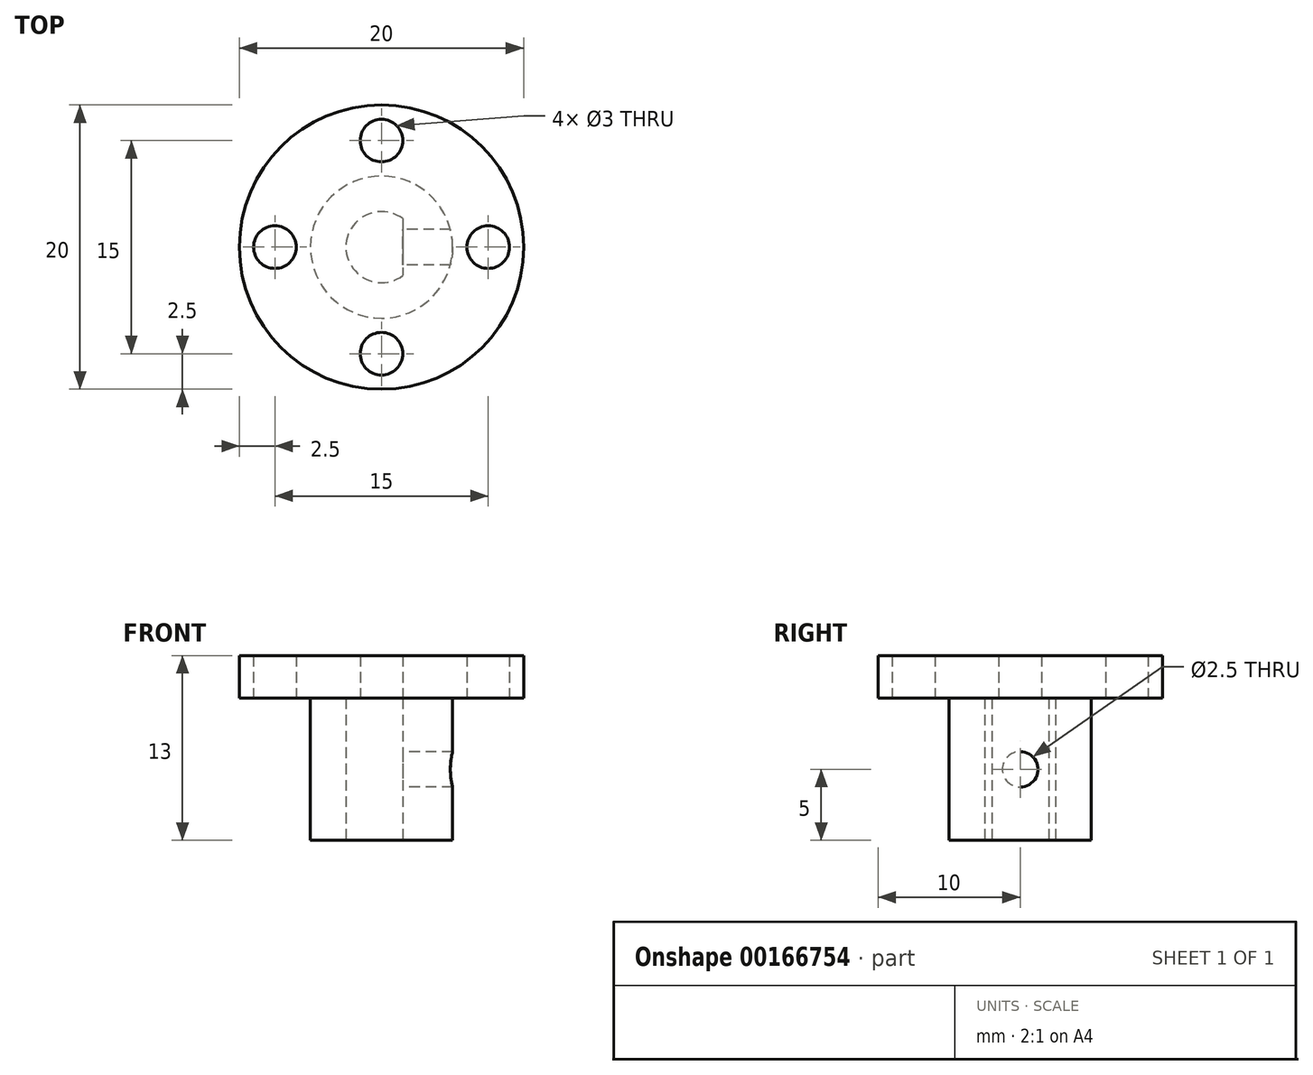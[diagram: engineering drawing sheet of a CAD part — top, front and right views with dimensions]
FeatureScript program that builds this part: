
annotation { "Feature Type Name" : "Feature", "Feature Type Description" : "" }
export const myFeature = defineFeature(function(context is Context, id is Id, definition is map)
    precondition{}
    {
        {
            var Q0;
            Q0=qCreatedBy(makeId("Top.planeOp"),FACE);
            var sketch = newSketch(context, id + "F0", { "sketchPlane" : qUnion([Q0])});
            skCircle(sketch, "E0", {"center": v(0, 0) * mm, "radius": 5 * mm});
            skCircle(sketch, "E1", {"center": v(0, 0) * mm, "radius": 2.5 * mm});
            skLineSegment(sketch, "E2", {"start": v(1.5, 2) * mm, "end": v(1.5, -2) * mm});
            skSolve(sketch);
        }
        {
            var Q0;
            Q0 = qSketchRegion(id + "F0", true);
            var Q1;
            {var subQ0=sQuery(id+"F0.wireOp",EDGE,"E2");Q1=makeQuery(id+"F0.imprint","IMPRINT",FACE,{"disambiguationData":[TD([[makeQuery(id+"F0.imprint","IMPRINT",EDGE,{"derivedFrom":subQ0}),1.0]])]});}
            extrude(context, id + "F1", {"entities" : qUnion([Q0, Q1]), "depth" : 10 * mm});
        }
        {
            var Q0;
            Q0=makeQuery(id+"F1.opExtrude","SWEPT_FACE",FACE,{"disambiguationData":[OSD([sQuery(id+"F0.wireOp",EDGE,"E2")])]});
            var sketch = newSketch(context, id + "F2", { "sketchPlane" : qUnion([Q0])});
            skCircle(sketch, "E3", {"center": v(0, 5) * mm, "radius": 1.25 * mm});
            skSolve(sketch);
        }
        {
            var Q0;
            Q0=makeQuery(id+"F2.imprint","IMPRINT",FACE,{"disambiguationData":[TD([[makeQuery(id+"F2.imprint","IMPRINT",EDGE,{"derivedFrom":sQuery(id+"F2.wireOp",EDGE,"E3")}),1.0]])]});
            extrude(context, id + "F3", {"entities" : qUnion([Q0]), "operationType" : NewBodyOperationType.REMOVE, "endBound" : BoundingType.UP_TO_NEXT, "oppositeDirection" : true, "depth" : 25 * mm});
        }
        {
            var Q0;
            Q0=makeQuery(id+"F1.opExtrude","CAP_FACE",FACE,{"disambiguationData":[OSD([sQuery(id+"F0.wireOp",EDGE,"E0"),sQuery(id+"F0.wireOp",EDGE,"E1"),sQuery(id+"F0.wireOp",EDGE,"E2")])],"isStart":false});
            var sketch = newSketch(context, id + "F4", { "sketchPlane" : qUnion([Q0])});
            skCircle(sketch, "E4", {"center": v(0, 0) * mm, "radius": 10 * mm});
            skCircle(sketch, "E5", {"center": v(0, 7.5) * mm, "radius": 1.5 * mm});
            skCircle(sketch, "E6.1.0", {"center": v(-7.5, 0) * mm, "radius": 1.5 * mm});
            skCircle(sketch, "E6.2.0", {"center": v(0, -7.5) * mm, "radius": 1.5 * mm});
            skCircle(sketch, "E6.3.0", {"center": v(7.5, 0) * mm, "radius": 1.5 * mm});
            skSolve(sketch);
        }
        {
            var Q0;
            Q0=makeQuery(id+"F4.imprint","IMPRINT",FACE,{"disambiguationData":[TD([[makeQuery(id+"F4.imprint","IMPRINT",EDGE,{"derivedFrom":sQuery(id+"F4.wireOp",EDGE,"E4")}),1.0]])]});
            var Q1;
            Q1=makeQuery(id+"F4.imprint","IMPRINT",FACE,{"disambiguationData":[TD([[makeQuery(id+"F4.imprint","IMPRINT",EDGE,{"derivedFrom":makeQuery(id+"F1.opExtrude","CAP_EDGE",EDGE,{"disambiguationData":[OSD([sQuery(id+"F0.wireOp",EDGE,"E0")])],"isStart":false})}),1.0]])]});
            var Q2;
            Q2=makeQuery(id+"F4.imprint","IMPRINT",FACE,{"disambiguationData":[TD([[makeQuery(id+"F4.imprint","IMPRINT",EDGE,{"derivedFrom":makeQuery(id+"F1.opExtrude","CAP_EDGE",EDGE,{"disambiguationData":[OSD([sQuery(id+"F0.wireOp",EDGE,"E1")])],"isStart":false})}),1.0]])]});
            extrude(context, id + "F5", {"entities" : qUnion([Q0, Q1, Q2]), "operationType" : NewBodyOperationType.ADD, "depth" : 3 * mm});
        }
    });
